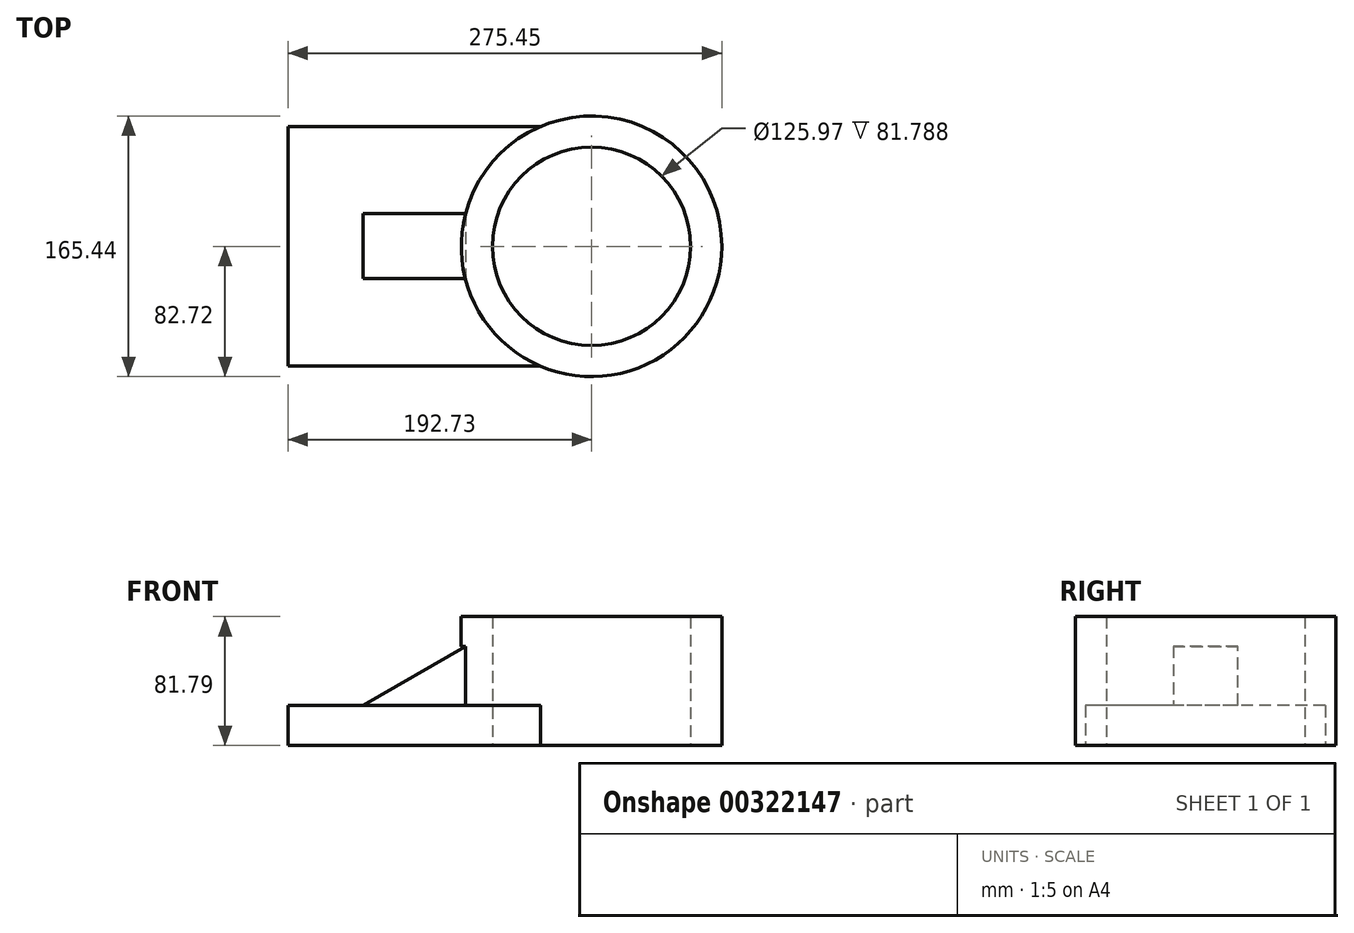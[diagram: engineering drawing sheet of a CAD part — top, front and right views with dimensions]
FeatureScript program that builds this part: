
annotation { "Feature Type Name" : "Feature", "Feature Type Description" : "" }
export const myFeature = defineFeature(function(context is Context, id is Id, definition is map)
    precondition{}
    {
        {
            var Q0;
            Q0=qCreatedBy(makeId("Top.planeOp"),FACE);
            var sketch = newSketch(context, id + "F0", { "sketchPlane" : qUnion([Q0])});
            skLineSegment(sketch, "E0.bottom", {"start": v(76.21, 76.2) * mm, "end": v(-116.81, 76.2) * mm});
            skLineSegment(sketch, "E0.top", {"start": v(76.21, -76.16) * mm, "end": v(-116.81, -76.16) * mm});
            skLineSegment(sketch, "E0.left", {"start": v(76.21, 76.2) * mm, "end": v(76.21, -76.16) * mm});
            skLineSegment(sketch, "E0.right", {"start": v(-116.81, 76.2) * mm, "end": v(-116.81, -76.16) * mm});
            skSolve(sketch);
        }
        {
            var Q0;
            Q0=makeQuery(id+"F0.imprint","IMPRINT",FACE,{"disambiguationData":[TD([[makeQuery(id+"F0.imprint","IMPRINT",EDGE,{"derivedFrom":sQuery(id+"F0.wireOp",EDGE,"E0.bottom")}),1.0]])]});
            var sketch = newSketch(context, id + "F1", { "sketchPlane" : qUnion([Q0])});
            skCircle(sketch, "E1", {"center": v(76.13, 0) * mm, "radius": 86.29 * mm});
            skCircle(sketch, "E2", {"center": v(76.13, 0) * mm, "radius": 63.3 * mm});
            skSolve(sketch);
        }
        {
            var Q0;
            Q0=makeQuery(id+"F0.imprint","IMPRINT",FACE,{"disambiguationData":[TD([[makeQuery(id+"F0.imprint","IMPRINT",EDGE,{"derivedFrom":sQuery(id+"F0.wireOp",EDGE,"E0.bottom")}),1.0]])]});
            extrude(context, id + "F2", {"entities" : qUnion([Q0]), "depth" : 25.4 * mm});
        }
        {
            var Q0;
            {var subQ0=sQuery(id+"F1.wireOp",EDGE,"E2");var subQ1=makeQuery(id+"F0.imprint","IMPRINT",EDGE,{"derivedFrom":sQuery(id+"F0.wireOp",EDGE,"E0.left")});var subQ2=makeQuery(id+"F1.imprint","INTERSECT",VERTEX,{"disambiguationData":[OD(0.0)],"derivedFrom":[subQ1,subQ0]});Q0=makeQuery(id+"F1.imprint","IMPRINT",FACE,{"disambiguationData":[TD([[makeQuery(id+"F1.imprint","IMPRINT",EDGE,{"disambiguationData":[TD([[subQ2,-1.0]])],"derivedFrom":subQ0}),1.0]])]});}
            extrude(context, id + "F3", {"entities" : qUnion([Q0]), "operationType" : NewBodyOperationType.REMOVE, "depth" : 82.04 * mm});
        }
        {
            var Q0;
            Q0=qCreatedBy(makeId("Top.planeOp"),FACE);
            var sketch = newSketch(context, id + "F4", { "sketchPlane" : qUnion([Q0])});
            skCircle(sketch, "E3", {"center": v(75.92, 0) * mm, "radius": 82.72 * mm});
            skCircle(sketch, "E4", {"center": v(75.92, 0) * mm, "radius": 62.98 * mm});
            skSolve(sketch);
        }
        {
            var Q0;
            Q0=makeQuery(id+"F4.imprint","IMPRINT",FACE,{"disambiguationData":[TD([[makeQuery(id+"F4.imprint","IMPRINT",EDGE,{"derivedFrom":sQuery(id+"F4.wireOp",EDGE,"E3")}),1.0]])]});
            extrude(context, id + "F5", {"entities" : qUnion([Q0]), "operationType" : NewBodyOperationType.ADD, "depth" : 81.8 * mm});
        }
        {
            var Q0;
            Q0=makeQuery(id+"F5.boolean.opBoolean","MERGE",FACE,{"derivedFrom":[makeQuery(id+"F2.opExtrude","CAP_FACE",FACE,{"disambiguationData":[OSD([sQuery(id+"F0.wireOp",EDGE,"E0.bottom"),sQuery(id+"F0.wireOp",EDGE,"E0.top"),sQuery(id+"F0.wireOp",EDGE,"E0.left"),sQuery(id+"F0.wireOp",EDGE,"E0.right")])],"isStart":true}),makeQuery(id+"F5.opExtrude","CAP_FACE",FACE,{"disambiguationData":[OSD([sQuery(id+"F4.wireOp",EDGE,"E3"),sQuery(id+"F4.wireOp",EDGE,"E4")])],"isStart":true})]});
            var sketch = newSketch(context, id + "F6", { "sketchPlane" : qUnion([Q0])});
            skLineSegment(sketch, "E5", {"start": v(0, 0) * mm, "end": v(8.54, 0) * mm});
            skLineSegment(sketch, "E6", {"start": v(8.54, 0) * mm, "end": v(8.54, -20.7) * mm});
            skLineSegment(sketch, "E7", {"start": v(8.54, 0) * mm, "end": v(8.54, 20.51) * mm});
            skLineSegment(sketch, "E8", {"start": v(8.54, 20.51) * mm, "end": v(-69.3, 20.51) * mm});
            skLineSegment(sketch, "E9", {"start": v(-69.3, 20.51) * mm, "end": v(-69.3, -20.7) * mm});
            skLineSegment(sketch, "E10", {"start": v(-69.3, -20.7) * mm, "end": v(8.54, -20.7) * mm});
            skSolve(sketch);
        }
        {
            var Q0;
            Q0=makeQuery(id+"F6.imprint","IMPRINT",FACE,{"disambiguationData":[TD([[makeQuery(id+"F6.imprint","IMPRINT",EDGE,{"derivedFrom":sQuery(id+"F6.wireOp",EDGE,"E6")}),-1.0]])]});
            extrude(context, id + "F7", {"entities" : qUnion([Q0]), "operationType" : NewBodyOperationType.ADD, "oppositeDirection" : true, "depth" : 63 * mm});
        }
        {
            var Q0;
            Q0=makeQuery(id+"F7.opExtrude","SWEPT_FACE",FACE,{"disambiguationData":[OSD([sQuery(id+"F6.wireOp",EDGE,"E8")])]});
            var sketch = newSketch(context, id + "F8", { "sketchPlane" : qUnion([Q0])});
            skLineSegment(sketch, "E11", {"start": v(-4.22, 63) * mm, "end": v(-69.3, 25.4) * mm});
            skLineSegment(sketch, "E12", {"start": v(-69.3, 25.4) * mm, "end": v(-69.3, 63) * mm});
            skLineSegment(sketch, "E13", {"start": v(-69.3, 63) * mm, "end": v(-4.22, 63) * mm});
            skSolve(sketch);
        }
        {
            var Q0;
            Q0=makeQuery(id+"F8.imprint","IMPRINT",FACE,{"disambiguationData":[TD([[makeQuery(id+"F8.imprint","IMPRINT",EDGE,{"derivedFrom":sQuery(id+"F8.wireOp",EDGE,"E11")}),-1.0]])]});
            extrude(context, id + "F9", {"entities" : qUnion([Q0]), "operationType" : NewBodyOperationType.REMOVE, "oppositeDirection" : true, "depth" : 46.23 * mm});
        }
    });
